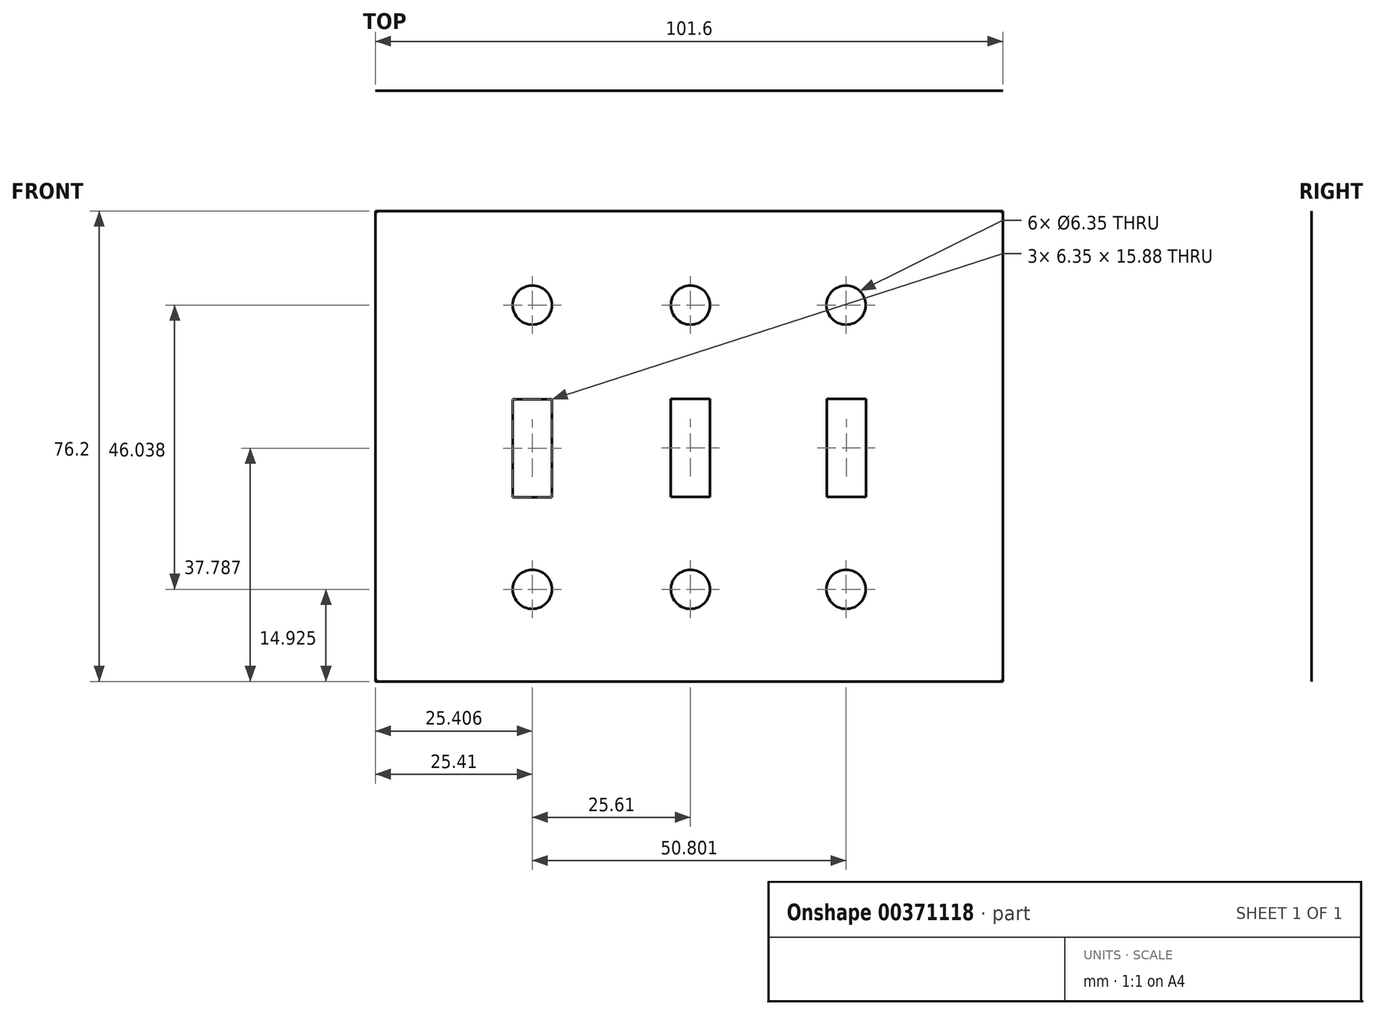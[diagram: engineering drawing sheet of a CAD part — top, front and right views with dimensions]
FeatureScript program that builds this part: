
annotation { "Feature Type Name" : "Feature", "Feature Type Description" : "" }
export const myFeature = defineFeature(function(context is Context, id is Id, definition is map)
    precondition{}
    {
        {
            var Q0;
            Q0=qCreatedBy(makeId("Front.planeOp"),FACE);
            var sketch = newSketch(context, id + "F0", { "sketchPlane" : qUnion([Q0])});
            skLineSegment(sketch, "E0.bottom", {"start": v(-51.02, 38.1) * mm, "end": v(50.58, 38.1) * mm});
            skLineSegment(sketch, "E0.top", {"start": v(-51.02, -38.1) * mm, "end": v(50.58, -38.1) * mm});
            skLineSegment(sketch, "E0.left", {"start": v(-51.02, 38.1) * mm, "end": v(-51.02, -38.1) * mm});
            skLineSegment(sketch, "E0.right", {"start": v(50.58, 38.1) * mm, "end": v(50.58, -38.1) * mm});
            skLineSegment(sketch, "E1", {"start": v(-51.02, 38.1) * mm, "end": v(-0.22, 38.1) * mm});
            skLineSegment(sketch, "E2", {"start": v(-51.02, 38.1) * mm, "end": v(-51.02, 0) * mm});
            skLineSegment(sketch, "E3.bottom", {"start": v(-3.18, 7.68) * mm, "end": v(3.17, 7.68) * mm});
            skLineSegment(sketch, "E3.top", {"start": v(-3.18, -8.2) * mm, "end": v(3.17, -8.2) * mm});
            skLineSegment(sketch, "E3.left", {"start": v(-3.18, 7.68) * mm, "end": v(-3.18, -8.2) * mm});
            skLineSegment(sketch, "E3.right", {"start": v(3.17, 7.68) * mm, "end": v(3.17, -8.2) * mm});
            skPoint(sketch, "E4.endSnap0", {"position": v(50.58, 0) * mm});
            skLineSegment(sketch, "E5.bottom", {"start": v(-28.79, 7.62) * mm, "end": v(-22.44, 7.62) * mm});
            skLineSegment(sketch, "E5.top", {"start": v(-28.79, -8.25) * mm, "end": v(-22.44, -8.25) * mm});
            skLineSegment(sketch, "E5.left", {"start": v(-28.79, 7.62) * mm, "end": v(-28.79, -8.25) * mm});
            skLineSegment(sketch, "E5.right", {"start": v(-22.44, 7.62) * mm, "end": v(-22.44, -8.25) * mm});
            skLineSegment(sketch, "E6.bottom", {"start": v(22.04, 7.68) * mm, "end": v(28.4, 7.68) * mm});
            skLineSegment(sketch, "E6.top", {"start": v(22.04, -8.2) * mm, "end": v(28.4, -8.2) * mm});
            skLineSegment(sketch, "E6.left", {"start": v(22.04, 7.68) * mm, "end": v(22.04, -8.2) * mm});
            skLineSegment(sketch, "E6.right", {"start": v(28.4, 7.68) * mm, "end": v(28.4, -8.2) * mm});
            skLineSegment(sketch, "E7", {"start": v(-51.02, -8.25) * mm, "end": v(-51.02, -38.1) * mm});
            skLineSegment(sketch, "E8", {"start": v(50.58, 38.1) * mm, "end": v(50.58, 7.62) * mm});
            skCircle(sketch, "E9", {"center": v(-25.6, 22.86) * mm, "radius": 3.18 * mm});
            skCircle(sketch, "E10", {"center": v(0, 22.86) * mm, "radius": 3.18 * mm});
            skCircle(sketch, "E11", {"center": v(25.2, 22.86) * mm, "radius": 3.18 * mm});
            skCircle(sketch, "E12", {"center": v(-25.6, -23.18) * mm, "radius": 3.18 * mm});
            skCircle(sketch, "E13", {"center": v(0, -23.18) * mm, "radius": 3.18 * mm});
            skCircle(sketch, "E14", {"center": v(25.2, -23.18) * mm, "radius": 3.18 * mm});
            skSolve(sketch);
        }
        {
            var Q0;
            Q0=makeQuery(id+"F0.imprint","IMPRINT",FACE,{"disambiguationData":[TD([[makeQuery(id+"F0.imprint","IMPRINT",EDGE,{"derivedFrom":sQuery(id+"F0.wireOp",EDGE,"E0.bottom")}),-1.0]])]});
            extrude(context, id + "F1", {"entities" : qUnion([Q0]), "depth" : 1 / 203.2 * mm});
        }
        {
            var Q0;
            Q0=makeQuery(id+"F1.opExtrude","CAP_EDGE",EDGE,{"disambiguationData":[OSD([sQuery(id+"F0.wireOp",EDGE,"E0.bottom"),sQuery(id+"F0.wireOp",EDGE,"E1")])],"isStart":false});
            fillet(context, id + "F2", {"entities" : qUnion([Q0]), "radius" : 6.35 * mm, "tangentPropagation" : true, "allowEdgeOverflow" : false});
        }
        {
            var Q0;
            Q0=makeQuery(id+"F1.opExtrude","CAP_EDGE",EDGE,{"disambiguationData":[OSD([sQuery(id+"F0.wireOp",EDGE,"E0.left"),sQuery(id+"F0.wireOp",EDGE,"E2"),sQuery(id+"F0.wireOp",EDGE,"E7")])],"isStart":false});
            fillet(context, id + "F3", {"entities" : qUnion([Q0]), "radius" : 6.35 * mm, "tangentPropagation" : true, "allowEdgeOverflow" : false});
        }
        {
            var Q0;
            Q0=makeQuery(id+"F1.opExtrude","CAP_EDGE",EDGE,{"disambiguationData":[OSD([sQuery(id+"F0.wireOp",EDGE,"E0.right"),sQuery(id+"F0.wireOp",EDGE,"E8")])],"isStart":false});
            fillet(context, id + "F4", {"entities" : qUnion([Q0]), "radius" : 6.35 * mm, "tangentPropagation" : true, "allowEdgeOverflow" : false});
        }
        {
            var Q0;
            Q0=makeQuery(id+"F1.opExtrude","CAP_EDGE",EDGE,{"disambiguationData":[OSD([sQuery(id+"F0.wireOp",EDGE,"E0.top")])],"isStart":false});
            fillet(context, id + "F5", {"entities" : qUnion([Q0]), "radius" : 6.35 * mm, "allowEdgeOverflow" : false});
        }
    });
